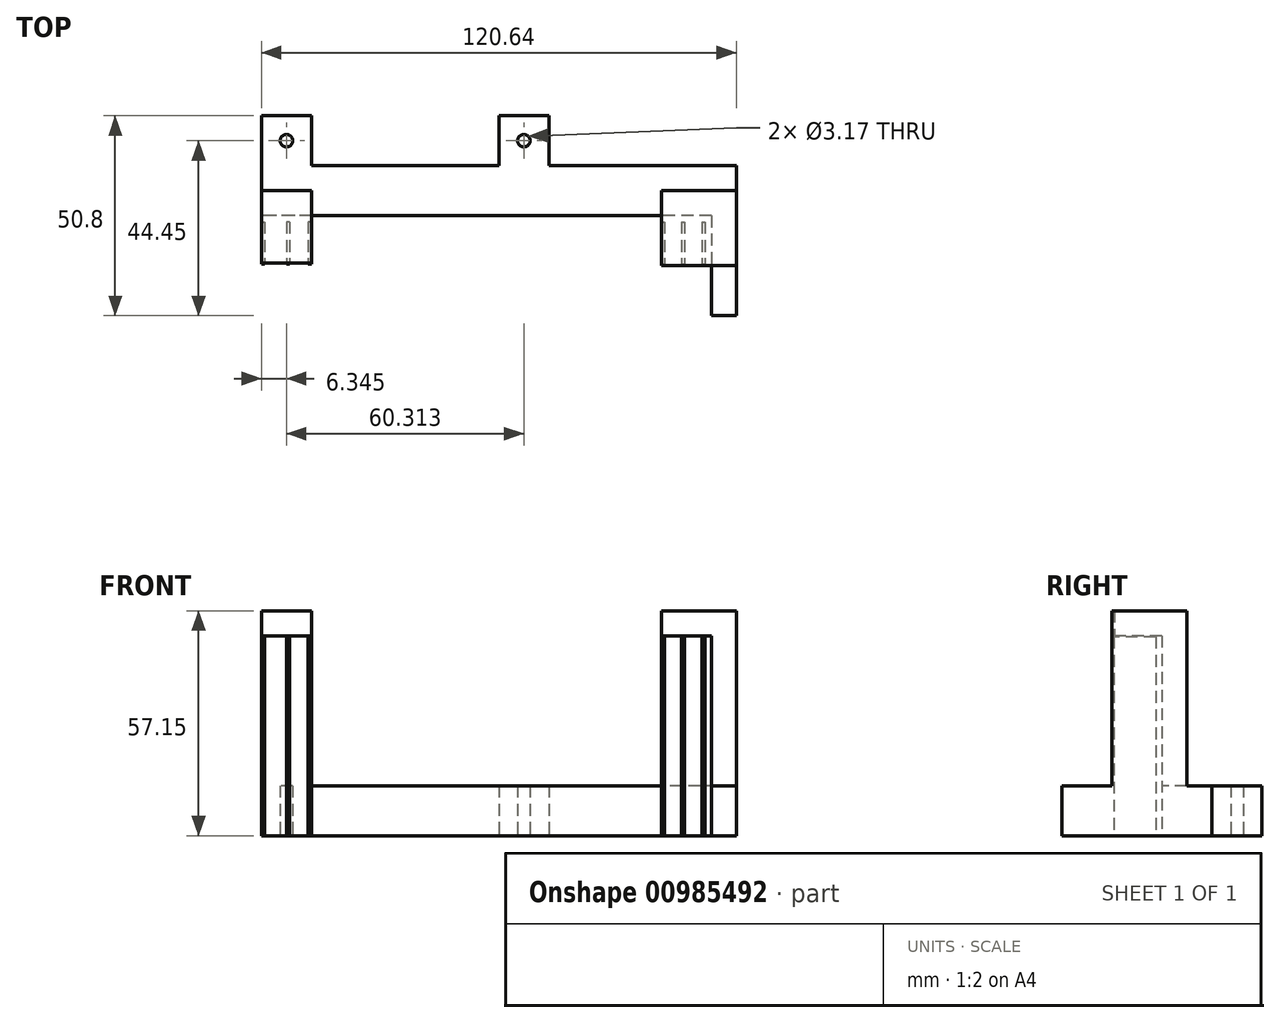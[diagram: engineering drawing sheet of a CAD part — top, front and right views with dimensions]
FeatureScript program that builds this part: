
annotation { "Feature Type Name" : "Feature", "Feature Type Description" : "" }
export const myFeature = defineFeature(function(context is Context, id is Id, definition is map)
    precondition{}
    {
        {
            var Q0;
            Q0=qCreatedBy(makeId("Top.planeOp"),FACE);
            var sketch = newSketch(context, id + "F0", { "sketchPlane" : qUnion([Q0])});
            skLineSegment(sketch, "E0.bottom", {"start": v(60.33, -6.35) * mm, "end": v(-60.33, -6.35) * mm});
            skLineSegment(sketch, "E0.top", {"start": v(60.33, 6.35) * mm, "end": v(-60.33, 6.35) * mm});
            skLineSegment(sketch, "E0.left", {"start": v(60.33, -6.35) * mm, "end": v(60.33, 6.35) * mm});
            skLineSegment(sketch, "E0.right", {"start": v(-60.33, -6.35) * mm, "end": v(-60.33, 6.35) * mm});
            skPoint(sketch, "E0.middle", {"position": v(0, 0) * mm});
            skLineSegment(sketch, "E1.bottom", {"start": v(60.33, -6.35) * mm, "end": v(53.98, -6.35) * mm});
            skLineSegment(sketch, "E1.top", {"start": v(60.33, -31.75) * mm, "end": v(53.98, -31.75) * mm});
            skLineSegment(sketch, "E1.left", {"start": v(60.32, -6.35) * mm, "end": v(60.33, -31.75) * mm});
            skLineSegment(sketch, "E1.right", {"start": v(53.98, -6.35) * mm, "end": v(53.98, -31.75) * mm});
            skLineSegment(sketch, "E2.bottom", {"start": v(-60.33, 6.35) * mm, "end": v(-47.63, 6.35) * mm});
            skLineSegment(sketch, "E2.top", {"start": v(-60.33, 19.05) * mm, "end": v(-47.63, 19.05) * mm});
            skLineSegment(sketch, "E2.left", {"start": v(-60.33, 6.35) * mm, "end": v(-60.33, 19.05) * mm});
            skLineSegment(sketch, "E2.right", {"start": v(-47.63, 6.35) * mm, "end": v(-47.63, 19.05) * mm});
            skLineSegment(sketch, "E3.bottom", {"start": v(0, 6.35) * mm, "end": v(12.7, 6.35) * mm});
            skLineSegment(sketch, "E3.top", {"start": v(0, 19.05) * mm, "end": v(12.7, 19.05) * mm});
            skLineSegment(sketch, "E3.left", {"start": v(0, 6.35) * mm, "end": v(0, 19.05) * mm});
            skLineSegment(sketch, "E3.right", {"start": v(12.7, 6.35) * mm, "end": v(12.7, 19.05) * mm});
            skCircle(sketch, "E4", {"center": v(-53.98, 12.7) * mm, "radius": 1.59 * mm});
            skCircle(sketch, "E5", {"center": v(6.34, 12.7) * mm, "radius": 1.59 * mm});
            skPoint(sketch, "E5.centerSnap0", {"position": v(0, 12.7) * mm});
            skLineSegment(sketch, "E6.bottom", {"start": v(-60.33, -7.94) * mm, "end": v(-59.53, -7.94) * mm});
            skLineSegment(sketch, "E6.top", {"start": v(-60.33, -18.6) * mm, "end": v(-59.53, -18.6) * mm});
            skLineSegment(sketch, "E6.left", {"start": v(-60.33, -7.94) * mm, "end": v(-60.33, -18.6) * mm});
            skLineSegment(sketch, "E6.right", {"start": v(-59.53, -7.94) * mm, "end": v(-59.53, -18.6) * mm});
            skLineSegment(sketch, "E7.bottom", {"start": v(-47.62, -7.94) * mm, "end": v(-48.42, -7.94) * mm});
            skLineSegment(sketch, "E7.top", {"start": v(-47.62, -18.6) * mm, "end": v(-48.42, -18.6) * mm});
            skLineSegment(sketch, "E7.left", {"start": v(-47.63, -7.94) * mm, "end": v(-47.63, -18.6) * mm});
            skLineSegment(sketch, "E7.right", {"start": v(-48.42, -7.94) * mm, "end": v(-48.42, -18.6) * mm});
            skLineSegment(sketch, "E8.bottom", {"start": v(-53.18, -7.94) * mm, "end": v(-53.98, -7.94) * mm});
            skLineSegment(sketch, "E8.top", {"start": v(-53.18, -18.6) * mm, "end": v(-53.98, -18.6) * mm});
            skLineSegment(sketch, "E8.left", {"start": v(-53.18, -7.94) * mm, "end": v(-53.18, -18.6) * mm});
            skLineSegment(sketch, "E8.right", {"start": v(-53.98, -7.94) * mm, "end": v(-53.98, -18.6) * mm});
            skLineSegment(sketch, "E9.bottom", {"start": v(41.27, -7.94) * mm, "end": v(42.07, -7.94) * mm});
            skLineSegment(sketch, "E9.top", {"start": v(41.27, -18.6) * mm, "end": v(42.07, -18.6) * mm});
            skLineSegment(sketch, "E9.left", {"start": v(41.27, -7.94) * mm, "end": v(41.27, -18.6) * mm});
            skLineSegment(sketch, "E9.right", {"start": v(42.07, -7.94) * mm, "end": v(42.07, -18.6) * mm});
            skLineSegment(sketch, "E10.bottom", {"start": v(46.35, -7.94) * mm, "end": v(47.15, -7.94) * mm});
            skLineSegment(sketch, "E10.top", {"start": v(46.36, -18.6) * mm, "end": v(47.15, -18.6) * mm});
            skLineSegment(sketch, "E10.left", {"start": v(46.35, -7.94) * mm, "end": v(46.36, -18.6) * mm});
            skLineSegment(sketch, "E10.right", {"start": v(47.15, -7.94) * mm, "end": v(47.15, -18.6) * mm});
            skLineSegment(sketch, "E11.bottom", {"start": v(51.6, -7.94) * mm, "end": v(52.39, -7.94) * mm});
            skLineSegment(sketch, "E11.top", {"start": v(51.6, -18.6) * mm, "end": v(52.39, -18.6) * mm});
            skLineSegment(sketch, "E11.left", {"start": v(51.6, -7.94) * mm, "end": v(51.6, -18.6) * mm});
            skLineSegment(sketch, "E11.right", {"start": v(52.39, -7.94) * mm, "end": v(52.39, -18.6) * mm});
            skSolve(sketch);
        }
        {
            var Q0;
            Q0=makeQuery(id+"F0.imprint","IMPRINT",FACE,{"disambiguationData":[TD([[makeQuery(id+"F0.imprint","IMPRINT",EDGE,{"derivedFrom":sQuery(id+"F0.wireOp",EDGE,"E2.top")}),-1.0]])]});
            var Q1;
            {var subQ0=sQuery(id+"F0.wireOp",EDGE,"E0.left");Q1=makeQuery(id+"F0.imprint","IMPRINT",FACE,{"disambiguationData":[TD([[makeQuery(id+"F0.imprint","IMPRINT",EDGE,{"derivedFrom":subQ0}),1.0]])]});}
            var Q2;
            Q2=makeQuery(id+"F0.imprint","IMPRINT",FACE,{"disambiguationData":[TD([[makeQuery(id+"F0.imprint","IMPRINT",EDGE,{"derivedFrom":sQuery(id+"F0.wireOp",EDGE,"E3.top")}),-1.0]])]});
            var Q3;
            Q3=makeQuery(id+"F0.imprint","IMPRINT",FACE,{"disambiguationData":[TD([[makeQuery(id+"F0.imprint","IMPRINT",EDGE,{"derivedFrom":sQuery(id+"F0.wireOp",EDGE,"E1.top")}),-1.0]])]});
            extrude(context, id + "F1", {"entities" : qUnion([Q0, Q1, Q2, Q3]), "depth" : 12.7 * mm, "offsetDistance" : 25.4 * mm});
        }
        {
            var Q0;
            Q0=makeQuery(id+"F0.imprint","IMPRINT",FACE,{"disambiguationData":[TD([[makeQuery(id+"F0.imprint","IMPRINT",EDGE,{"derivedFrom":sQuery(id+"F0.wireOp",EDGE,"E6.bottom")}),-1.0]])]});
            var Q1;
            Q1=makeQuery(id+"F0.imprint","IMPRINT",FACE,{"disambiguationData":[TD([[makeQuery(id+"F0.imprint","IMPRINT",EDGE,{"derivedFrom":sQuery(id+"F0.wireOp",EDGE,"E8.bottom")}),1.0]])]});
            var Q2;
            Q2=makeQuery(id+"F0.imprint","IMPRINT",FACE,{"disambiguationData":[TD([[makeQuery(id+"F0.imprint","IMPRINT",EDGE,{"derivedFrom":sQuery(id+"F0.wireOp",EDGE,"E7.bottom")}),1.0]])]});
            var Q3;
            Q3=makeQuery(id+"F0.imprint","IMPRINT",FACE,{"disambiguationData":[TD([[makeQuery(id+"F0.imprint","IMPRINT",EDGE,{"derivedFrom":sQuery(id+"F0.wireOp",EDGE,"E9.bottom")}),-1.0]])]});
            var Q4;
            Q4=makeQuery(id+"F0.imprint","IMPRINT",FACE,{"disambiguationData":[TD([[makeQuery(id+"F0.imprint","IMPRINT",EDGE,{"derivedFrom":sQuery(id+"F0.wireOp",EDGE,"E10.bottom")}),-1.0]])]});
            var Q5;
            Q5=makeQuery(id+"F0.imprint","IMPRINT",FACE,{"disambiguationData":[TD([[makeQuery(id+"F0.imprint","IMPRINT",EDGE,{"derivedFrom":sQuery(id+"F0.wireOp",EDGE,"E11.bottom")}),-1.0]])]});
            extrude(context, id + "F2", {"entities" : qUnion([Q0, Q1, Q2, Q3, Q4, Q5]), "depth" : 50.55 * mm, "offsetDistance" : 25.4 * mm});
        }
        {
            var Q0;
            Q0=makeQuery(id+"F1.opExtrude","CAP_FACE",FACE,{"disambiguationData":[OSD([sQuery(id+"F0.wireOp",EDGE,"E0.bottom"),sQuery(id+"F0.wireOp",EDGE,"E0.top"),sQuery(id+"F0.wireOp",EDGE,"E0.left"),sQuery(id+"F0.wireOp",EDGE,"E0.right"),sQuery(id+"F0.wireOp",EDGE,"E1.top"),sQuery(id+"F0.wireOp",EDGE,"E1.left"),sQuery(id+"F0.wireOp",EDGE,"E1.right"),sQuery(id+"F0.wireOp",EDGE,"E2.top"),sQuery(id+"F0.wireOp",EDGE,"E2.left"),sQuery(id+"F0.wireOp",EDGE,"E2.right"),sQuery(id+"F0.wireOp",EDGE,"E3.top"),sQuery(id+"F0.wireOp",EDGE,"E3.left"),sQuery(id+"F0.wireOp",EDGE,"E3.right"),sQuery(id+"F0.wireOp",EDGE,"E4"),sQuery(id+"F0.wireOp",EDGE,"E5")])],"isStart":false});
            var sketch = newSketch(context, id + "F3", { "sketchPlane" : qUnion([Q0])});
            skLineSegment(sketch, "E12.bottom", {"start": v(-60.33, 0) * mm, "end": v(-47.62, 0) * mm});
            skLineSegment(sketch, "E12.top", {"start": v(-60.33, -6.35) * mm, "end": v(-47.62, -6.35) * mm});
            skLineSegment(sketch, "E12.left", {"start": v(-60.33, 0) * mm, "end": v(-60.33, -6.35) * mm});
            skLineSegment(sketch, "E12.right", {"start": v(-47.62, 0) * mm, "end": v(-47.62, -6.35) * mm});
            skLineSegment(sketch, "E13.bottom", {"start": v(53.98, 0) * mm, "end": v(41.27, 0) * mm});
            skLineSegment(sketch, "E13.top", {"start": v(53.98, -6.35) * mm, "end": v(41.27, -6.35) * mm});
            skLineSegment(sketch, "E13.left", {"start": v(53.98, 0) * mm, "end": v(53.98, -6.35) * mm});
            skLineSegment(sketch, "E13.right", {"start": v(41.27, 0) * mm, "end": v(41.27, -6.35) * mm});
            skLineSegment(sketch, "E14.bottom", {"start": v(53.98, 0) * mm, "end": v(60.33, 0) * mm});
            skLineSegment(sketch, "E14.top", {"start": v(53.98, -19.05) * mm, "end": v(60.33, -19.05) * mm});
            skLineSegment(sketch, "E14.left", {"start": v(53.98, 0) * mm, "end": v(53.98, -19.05) * mm});
            skLineSegment(sketch, "E14.right", {"start": v(60.33, 0) * mm, "end": v(60.33, -19.05) * mm});
            skSolve(sketch);
        }
        {
            var Q0;
            Q0=makeQuery(id+"F3.imprint","IMPRINT",FACE,{"disambiguationData":[TD([[makeQuery(id+"F3.imprint","IMPRINT",EDGE,{"derivedFrom":sQuery(id+"F3.wireOp",EDGE,"E12.bottom")}),-1.0]])]});
            var Q1;
            {var subQ0=sQuery(id+"F3.wireOp",EDGE,"E13.bottom");Q1=makeQuery(id+"F3.imprint","IMPRINT",FACE,{"disambiguationData":[TD([[makeQuery(id+"F3.imprint","IMPRINT",EDGE,{"derivedFrom":subQ0}),1.0]])]});}
            var Q2;
            {var subQ2=sQuery(id+"F3.wireOp",EDGE,"E14.bottom");Q2=makeQuery(id+"F3.imprint","IMPRINT",FACE,{"disambiguationData":[TD([[makeQuery(id+"F3.imprint","IMPRINT",EDGE,{"derivedFrom":subQ2}),-1.0]])]});}
            extrude(context, id + "F4", {"entities" : qUnion([Q0, Q1, Q2]), "operationType" : NewBodyOperationType.ADD, "depth" : 38.1 * mm, "offsetDistance" : 25.4 * mm});
        }
        {
            var Q0;
            Q0=makeQuery(id+"F4.opExtrude","CAP_FACE",FACE,{"disambiguationData":[OSD([sQuery(id+"F3.wireOp",EDGE,"E12.bottom"),sQuery(id+"F3.wireOp",EDGE,"E12.top"),sQuery(id+"F3.wireOp",EDGE,"E12.left"),sQuery(id+"F3.wireOp",EDGE,"E12.right")])],"isStart":false});
            var sketch = newSketch(context, id + "F5", { "sketchPlane" : qUnion([Q0])});
            skLineSegment(sketch, "E15.bottom", {"start": v(-60.32, 0) * mm, "end": v(-47.62, 0) * mm});
            skLineSegment(sketch, "E15.top", {"start": v(-60.32, -18.41) * mm, "end": v(-47.62, -18.41) * mm});
            skLineSegment(sketch, "E15.left", {"start": v(-60.32, 0) * mm, "end": v(-60.32, -18.41) * mm});
            skLineSegment(sketch, "E15.right", {"start": v(-47.62, 0) * mm, "end": v(-47.62, -18.41) * mm});
            skSolve(sketch);
        }
        {
            var Q0;
            {var subQ0=sQuery(id+"F5.wireOp",EDGE,"E15.top");Q0=makeQuery(id+"F5.imprint","IMPRINT",FACE,{"disambiguationData":[TD([[makeQuery(id+"F5.imprint","IMPRINT",EDGE,{"derivedFrom":subQ0}),1.0]])]});}
            var Q1;
            {var subQ0=sQuery(id+"F5.wireOp",EDGE,"E15.bottom");Q1=makeQuery(id+"F5.imprint","IMPRINT",FACE,{"disambiguationData":[TD([[makeQuery(id+"F5.imprint","IMPRINT",EDGE,{"derivedFrom":subQ0}),-1.0]])]});}
            extrude(context, id + "F6", {"entities" : qUnion([Q0, Q1]), "operationType" : NewBodyOperationType.ADD, "depth" : 6.35 * mm, "offsetDistance" : 25.4 * mm});
        }
        {
            var Q0;
            Q0=makeQuery(id+"F4.opExtrude","CAP_FACE",FACE,{"disambiguationData":[OSD([sQuery(id+"F3.wireOp",EDGE,"E13.bottom"),sQuery(id+"F3.wireOp",EDGE,"E13.top"),sQuery(id+"F3.wireOp",EDGE,"E13.right"),sQuery(id+"F3.wireOp",EDGE,"E14.bottom"),sQuery(id+"F3.wireOp",EDGE,"E14.top"),sQuery(id+"F3.wireOp",EDGE,"E14.left"),sQuery(id+"F3.wireOp",EDGE,"E14.right")])],"isStart":false});
            var sketch = newSketch(context, id + "F7", { "sketchPlane" : qUnion([Q0])});
            skLineSegment(sketch, "E16.bottom", {"start": v(60.33, 0) * mm, "end": v(41.27, 0) * mm});
            skLineSegment(sketch, "E16.top", {"start": v(60.33, -19.05) * mm, "end": v(41.27, -19.05) * mm});
            skLineSegment(sketch, "E16.left", {"start": v(60.33, 0) * mm, "end": v(60.33, -19.05) * mm});
            skLineSegment(sketch, "E16.right", {"start": v(41.27, 0) * mm, "end": v(41.27, -19.05) * mm});
            skSolve(sketch);
        }
        {
            var Q0;
            {var subQ4=sQuery(id+"F7.wireOp",EDGE,"E16.bottom");Q0=makeQuery(id+"F7.imprint","IMPRINT",FACE,{"disambiguationData":[TD([[makeQuery(id+"F7.imprint","IMPRINT",EDGE,{"derivedFrom":subQ4}),1.0]])]});}
            var Q1;
            {var subQ4=makeQuery(id+"F4.opExtrude","CAP_EDGE",EDGE,{"disambiguationData":[OSD([sQuery(id+"F3.wireOp",EDGE,"E13.top")])],"isStart":false});Q1=makeQuery(id+"F7.imprint","IMPRINT",FACE,{"disambiguationData":[TD([[makeQuery(id+"F7.imprint","IMPRINT",EDGE,{"derivedFrom":subQ4}),1.0]])]});}
            extrude(context, id + "F8", {"entities" : qUnion([Q0, Q1]), "operationType" : NewBodyOperationType.ADD, "depth" : 6.35 * mm, "offsetDistance" : 25.4 * mm});
        }
    });
